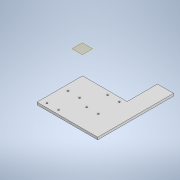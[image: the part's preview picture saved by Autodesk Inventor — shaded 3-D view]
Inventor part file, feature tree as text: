
AUTODESK INVENTOR PART (.ipt)
format: ipt  version: 2020 (Build 240168000, 168)  size: 139,264 bytes
history: native  units: mm
features: other x2, sketch x2, extrude x1, hole x1, projected_geometry x1
ambient origin geometry x8: Origin, YZ Plane, XZ Plane, XY Plane, X Axis, Y Axis, Z Axis, Center Point
bodies: Body1 (feature_tree)
feature tree (7):
  other  "작업 평면1"
  extrude  "돌출1"  Depth=10.0mm
  hole  "구멍1"  [1 undecoded]
  sketch  "스케치1"
  sketch  "스케치3"
  projected_geometry  "투영된 루프3"
  other  "솔리드1"
note: 1 required parameter value undecoded (feature->parameter linkage not recoverable at this tier; creation-order binding heuristic only, values carry confidence <= 0.55)
